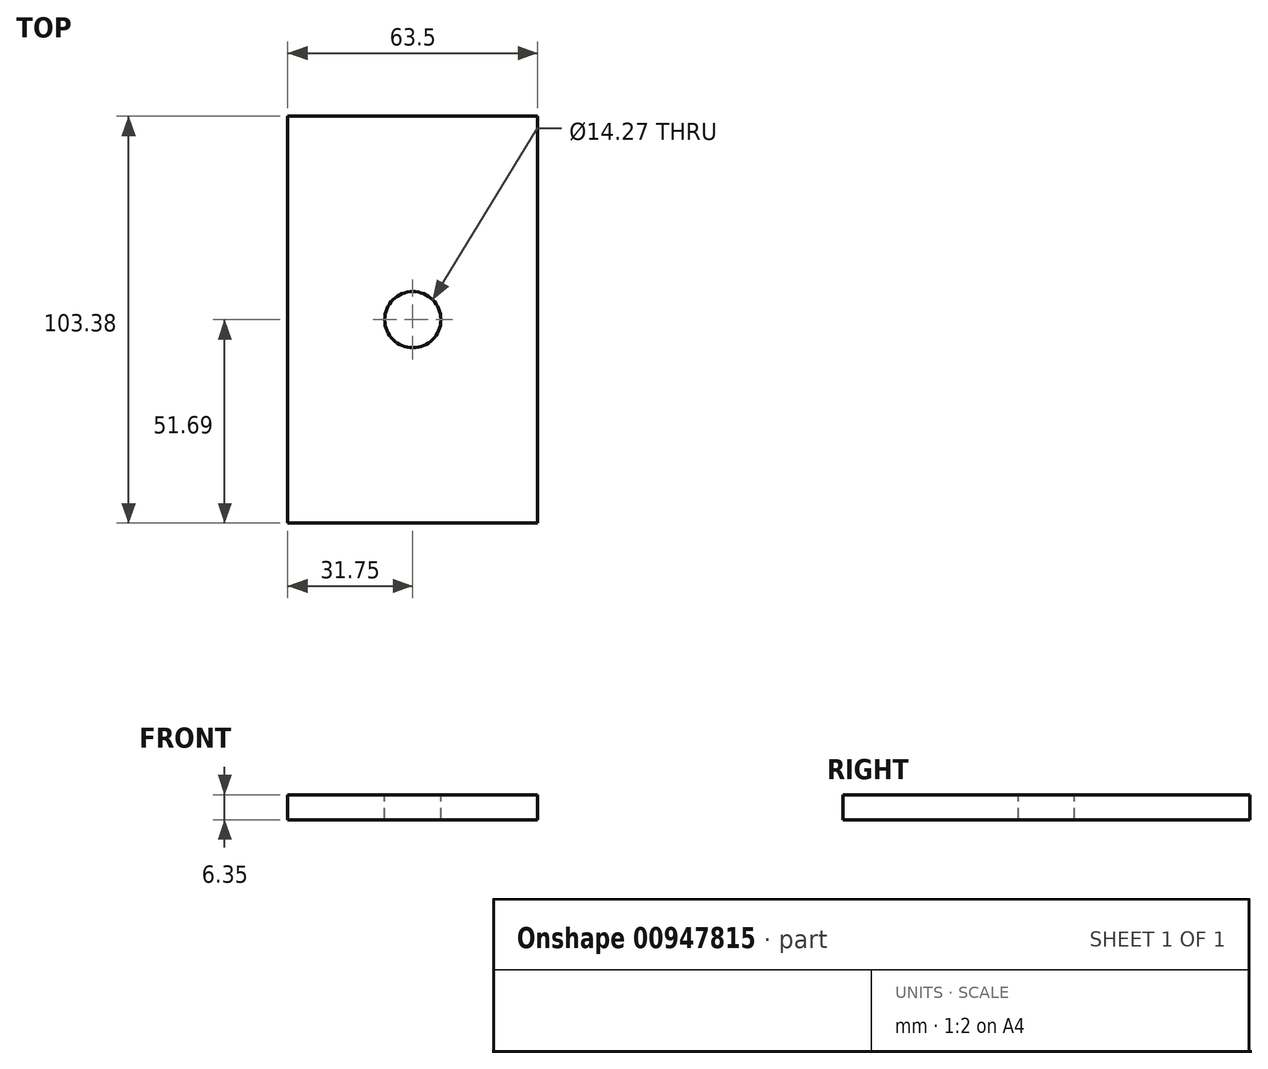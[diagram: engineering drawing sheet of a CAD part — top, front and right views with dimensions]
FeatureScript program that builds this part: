
annotation { "Feature Type Name" : "Feature", "Feature Type Description" : "" }
export const myFeature = defineFeature(function(context is Context, id is Id, definition is map)
    precondition{}
    {
        {
            var Q0;
            Q0=qCreatedBy(makeId("Top.planeOp"),FACE);
            var sketch = newSketch(context, id + "F0", { "sketchPlane" : qUnion([Q0])});
            skPoint(sketch, "E0", {"position": v(0, 0) * mm});
            skLineSegment(sketch, "E1.bottom", {"start": v(-31.75, -51.69) * mm, "end": v(31.75, -51.69) * mm});
            skLineSegment(sketch, "E1.top", {"start": v(-31.75, 51.69) * mm, "end": v(31.75, 51.69) * mm});
            skLineSegment(sketch, "E1.left", {"start": v(-31.75, -51.69) * mm, "end": v(-31.75, 51.69) * mm});
            skLineSegment(sketch, "E1.right", {"start": v(31.75, -51.69) * mm, "end": v(31.75, 51.69) * mm});
            skSolve(sketch);
        }
        {
            var Q0;
            Q0 = qSketchRegion(id + "F0", true);
            extrude(context, id + "F1", {"entities" : qUnion([Q0]), "depth" : 6.35 * mm, "offsetDistance" : 25 * mm});
        }
        {
            var Q0;
            Q0=sQuery(id+"F0.wireOp",VERTEX,"E0");
            var Q1;
            Q1=makeQuery(id+"F1.opExtrude","SWEPT_BODY",BODY,{"disambiguationData":[OSD([sQuery(id+"F0.wireOp",EDGE,"E1.bottom"),sQuery(id+"F0.wireOp",EDGE,"E1.top"),sQuery(id+"F0.wireOp",EDGE,"E1.left"),sQuery(id+"F0.wireOp",EDGE,"E1.right")])]});
            hole(context, id + "F2", {"style" : HoleStyle.SIMPLE, "endStyle" : HoleEndStyle.THROUGH, "oppositeDirection" : true, "standardTappedOrClearance" : lookupTablePath({ "fit" : "Normal (ASME)", "standard" : "ANSI", "size" : "1/2", "type" : "Clearance" }), "standardBlindInLast" : lookupTablePath({ "fit" : "Normal", "standard" : "ANSI", "engagement" : "75%", "pitch" : "13 tpi", "size" : "1/2", "type" : "Clearance & tapped" }), "holeDiameter" : 14.27 * mm, "majorDiameter" : 5 * mm, "isTappedThrough" : true, "tappedDepth" : 40.45 * mm, "tapClearance" : 3, "locations" : qUnion([Q0]), "scope" : qUnion([Q1]), "startStyle" : HoleStartStyle.SKETCH});
        }
    });
